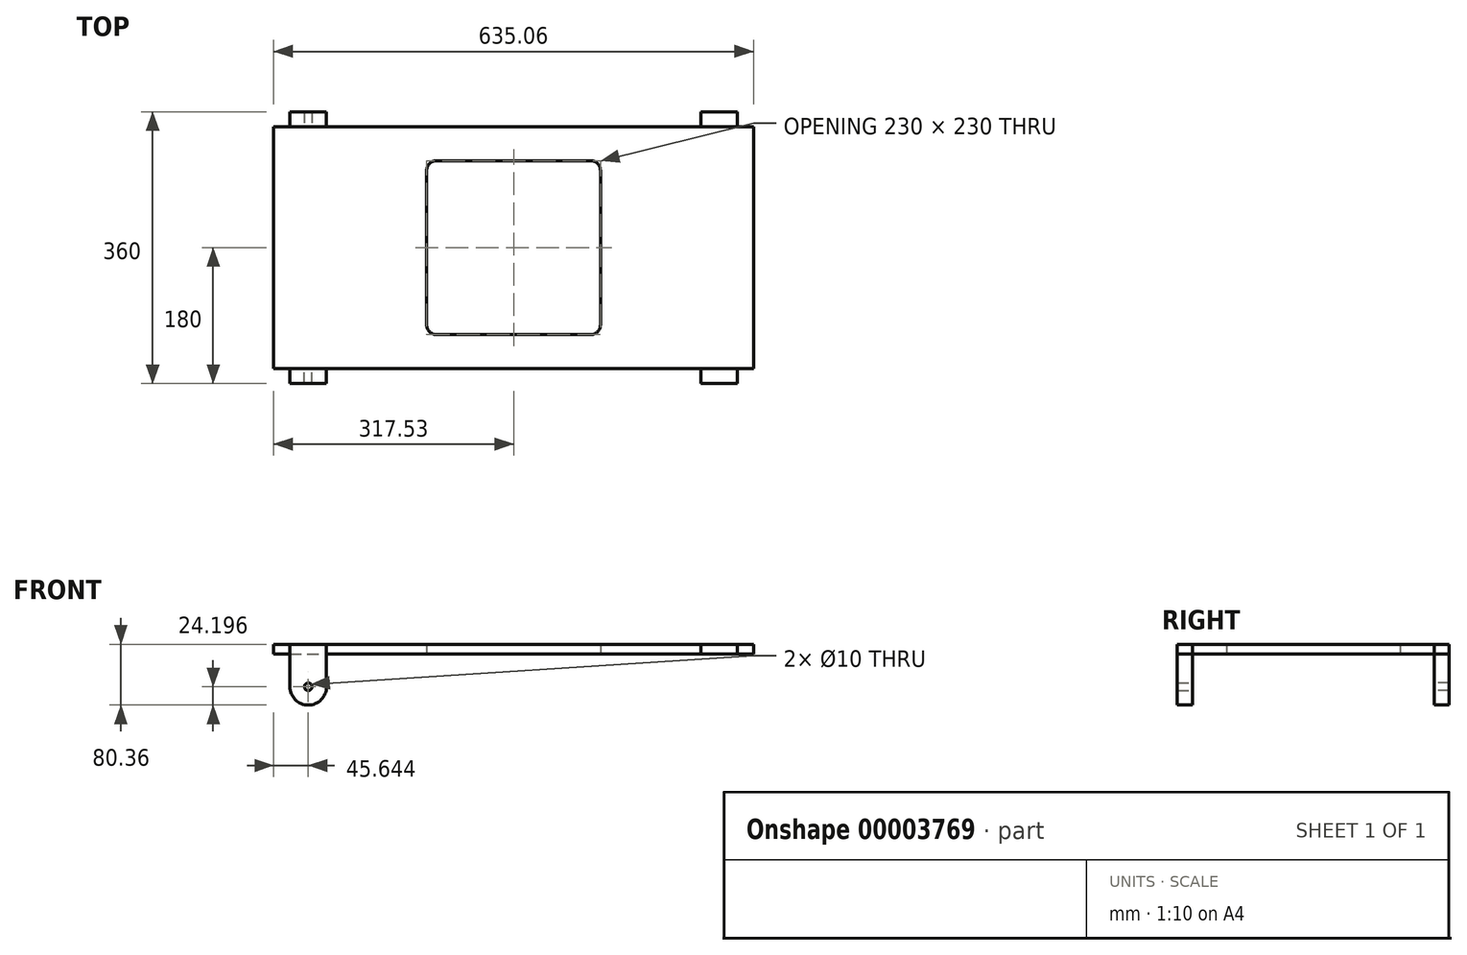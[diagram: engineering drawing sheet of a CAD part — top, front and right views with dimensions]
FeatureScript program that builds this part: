
annotation { "Feature Type Name" : "Feature", "Feature Type Description" : "" }
export const myFeature = defineFeature(function(context is Context, id is Id, definition is map)
    precondition{}
    {
        {
            var Q0;
            Q0=qCreatedBy(makeId("Top.planeOp"),FACE);
            var sketch = newSketch(context, id + "F0", { "sketchPlane" : qUnion([Q0])});
            skLineSegment(sketch, "E0.rect.bottom", {"start": v(-317.53, 160) * mm, "end": v(317.53, 160) * mm});
            skLineSegment(sketch, "E0.rect.top", {"start": v(-317.53, -160) * mm, "end": v(317.53, -160) * mm});
            skLineSegment(sketch, "E0.rect.left", {"start": v(-317.53, 160) * mm, "end": v(-317.53, -160) * mm});
            skLineSegment(sketch, "E0.rect.right", {"start": v(317.53, 160) * mm, "end": v(317.53, -160) * mm});
            skPoint(sketch, "E0.rect.middle", {"position": v(0, 0) * mm});
            skLineSegment(sketch, "E1.rect.bottom", {"start": v(-102.3, 115) * mm, "end": v(102.3, 115) * mm});
            skLineSegment(sketch, "E1.rect.top", {"start": v(-102.3, -115) * mm, "end": v(102.3, -115) * mm});
            skLineSegment(sketch, "E1.rect.left", {"start": v(-115, 102.3) * mm, "end": v(-115, -102.3) * mm});
            skLineSegment(sketch, "E1.rect.right", {"start": v(115, 102.3) * mm, "end": v(115, -102.3) * mm});
            skPoint(sketch, "E2.visualSharp", {"position": v(-115, 115) * mm});
            skArc(sketch, "E2.filletArc", {"start": v(-102.3, 115) * mm, "mid": v(-111.28, 111.28) * mm, "end": v(-115, 102.3) * mm});
            skPoint(sketch, "E3.visualSharp", {"position": v(115, 115) * mm});
            skArc(sketch, "E3.filletArc", {"start": v(115, 102.3) * mm, "mid": v(111.28, 111.28) * mm, "end": v(102.3, 115) * mm});
            skPoint(sketch, "E4.visualSharp", {"position": v(115, -115) * mm});
            skArc(sketch, "E4.filletArc", {"start": v(102.3, -115) * mm, "mid": v(111.28, -111.28) * mm, "end": v(115, -102.3) * mm});
            skPoint(sketch, "E5.visualSharp", {"position": v(-115, -115) * mm});
            skArc(sketch, "E5.filletArc", {"start": v(-115, -102.3) * mm, "mid": v(-111.28, -111.28) * mm, "end": v(-102.3, -115) * mm});
            skSolve(sketch);
        }
        {
            var Q0;
            Q0=makeQuery(id+"F0.imprint","IMPRINT",FACE,{"disambiguationData":[TD([[makeQuery(id+"F0.imprint","IMPRINT",EDGE,{"derivedFrom":sQuery(id+"F0.wireOp",EDGE,"E0.rect.bottom")}),-1.0]])]});
            extrude(context, id + "F1", {"entities" : qUnion([Q0]), "depth" : 12.7 * mm});
        }
        {
            var Q0;
            Q0=makeQuery(id+"F1.opExtrude","SWEPT_FACE",FACE,{"disambiguationData":[OSD([sQuery(id+"F0.wireOp",EDGE,"E0.rect.top")])]});
            var sketch = newSketch(context, id + "F2", { "sketchPlane" : qUnion([Q0])});
            skArc(sketch, "E6", {"start": v(-296.08, -43.46) * mm, "mid": v(-271.89, -67.66) * mm, "end": v(-247.69, -43.46) * mm});
            skLineSegment(sketch, "E7", {"start": v(-296.08, -43.46) * mm, "end": v(-296.08, 12.7) * mm});
            skLineSegment(sketch, "E8", {"start": v(-247.69, -43.46) * mm, "end": v(-247.69, 12.7) * mm});
            skCircle(sketch, "E9", {"center": v(-271.89, -43.46) * mm, "radius": 5 * mm});
            skLineSegment(sketch, "E10", {"start": v(0, 12.7) * mm, "end": v(0, 0) * mm, "construction": true});
            skLineSegment(sketch, "E11.0.MirrorCS", {"start": v(296.08, -43.46) * mm, "end": v(296.08, 12.7) * mm});
            skArc(sketch, "E12.0.MirrorCS", {"start": v(296.08, -43.46) * mm, "mid": v(271.89, -67.66) * mm, "end": v(247.69, -43.46) * mm});
            skLineSegment(sketch, "E13.0.MirrorCS", {"start": v(247.69, -43.46) * mm, "end": v(247.69, 12.7) * mm});
            skCircle(sketch, "E14.0.MirrorC", {"center": v(271.89, -43.46) * mm, "radius": 5 * mm});
            skSolve(sketch);
        }
        {
            var Q0;
            {var subQ0=sQuery(id+"F0.wireOp",EDGE,"E0.rect.top");var subQ4=sQuery(id+"F2.wireOp",EDGE,"E7");var subQ6=makeQuery(id+"F1.opExtrude","CAP_EDGE",EDGE,{"disambiguationData":[OSD([subQ0])],"isStart":false});var subQ8=makeQuery(id+"F2.imprint","INTERSECT",VERTEX,{"derivedFrom":[subQ6,subQ4]});Q0=makeQuery(id+"F2.imprint","IMPRINT",FACE,{"disambiguationData":[TD([[makeQuery(id+"F2.imprint","IMPRINT",EDGE,{"disambiguationData":[TD([[subQ8,1.0]])],"derivedFrom":subQ4}),-1.0]])]});}
            var Q1;
            {var subQ5=sQuery(id+"F2.wireOp",EDGE,"E6");Q1=makeQuery(id+"F2.imprint","IMPRINT",FACE,{"disambiguationData":[TD([[makeQuery(id+"F2.imprint","IMPRINT",EDGE,{"derivedFrom":subQ5}),1.0]])]});}
            var Q2;
            {var subQ0=sQuery(id+"F0.wireOp",EDGE,"E0.rect.top");var subQ4=sQuery(id+"F2.wireOp",EDGE,"E11.0.MirrorCS");var subQ6=makeQuery(id+"F1.opExtrude","CAP_EDGE",EDGE,{"disambiguationData":[OSD([subQ0])],"isStart":false});var subQ8=makeQuery(id+"F2.imprint","INTERSECT",VERTEX,{"derivedFrom":[subQ6,subQ4]});Q2=makeQuery(id+"F2.imprint","IMPRINT",FACE,{"disambiguationData":[TD([[makeQuery(id+"F2.imprint","IMPRINT",EDGE,{"disambiguationData":[TD([[subQ8,1.0]])],"derivedFrom":subQ4}),1.0]])]});}
            var Q3;
            {var subQ3=sQuery(id+"F2.wireOp",EDGE,"E12.0.MirrorCS");Q3=makeQuery(id+"F2.imprint","IMPRINT",FACE,{"disambiguationData":[TD([[makeQuery(id+"F2.imprint","IMPRINT",EDGE,{"derivedFrom":subQ3}),-1.0]])]});}
            extrude(context, id + "F3", {"entities" : qUnion([Q0, Q1, Q2, Q3]), "depth" : 20 * mm});
        }
        {
            var Q0;
            Q0=makeQuery(id+"F3.opExtrude","SWEPT_BODY",BODY,{"disambiguationData":[OSD([sQuery(id+"F0.wireOp",EDGE,"E0.rect.top"),sQuery(id+"F2.wireOp",EDGE,"E6"),sQuery(id+"F2.wireOp",EDGE,"E7"),sQuery(id+"F2.wireOp",EDGE,"E8"),sQuery(id+"F2.wireOp",EDGE,"E9")])]});
            var Q1;
            Q1=qCreatedBy(makeId("Front.planeOp"),FACE);
            mirror(context, id + "F4", {"entities" : qUnion([Q0]), "mirrorPlane" : qUnion([Q1])});
        }
        {
            var Q0;
            Q0=makeQuery(id+"F3.opExtrude","SWEPT_BODY",BODY,{"disambiguationData":[OSD([sQuery(id+"F0.wireOp",EDGE,"E0.rect.top"),sQuery(id+"F2.wireOp",EDGE,"E11.0.MirrorCS"),sQuery(id+"F2.wireOp",EDGE,"E12.0.MirrorCS"),sQuery(id+"F2.wireOp",EDGE,"E13.0.MirrorCS"),sQuery(id+"F2.wireOp",EDGE,"E14.0.MirrorC")])]});
            var Q1;
            Q1=qCreatedBy(makeId("Front.planeOp"),FACE);
            mirror(context, id + "F5", {"entities" : qUnion([Q0]), "mirrorPlane" : qUnion([Q1])});
        }
        {
            var Q0;
            Q0=makeQuery(id+"F5.opPattern","COPY",FACE,{"derivedFrom":makeQuery(id+"F3.opExtrude","CAP_FACE",FACE,{"disambiguationData":[OSD([sQuery(id+"F0.wireOp",EDGE,"E0.rect.top"),sQuery(id+"F2.wireOp",EDGE,"E11.0.MirrorCS"),sQuery(id+"F2.wireOp",EDGE,"E12.0.MirrorCS"),sQuery(id+"F2.wireOp",EDGE,"E13.0.MirrorCS"),sQuery(id+"F2.wireOp",EDGE,"E14.0.MirrorC")])],"isStart":false}),"instanceName":"1"});
            var sketch = newSketch(context, id + "F6", { "sketchPlane" : qUnion([Q0])});
            skCircle(sketch, "E15", {"center": v(-271.89, -43.46) * mm, "radius": 5 * mm});
            skCircle(sketch, "E16.0.MirrorC", {"center": v(271.89, -43.46) * mm, "radius": 5 * mm});
            skSolve(sketch);
        }
        {
            var Q0;
            Q0=makeQuery(id+"F6.imprint","IMPRINT",FACE,{"disambiguationData":[TD([[makeQuery(id+"F6.imprint","IMPRINT",EDGE,{"derivedFrom":sQuery(id+"F6.wireOp",EDGE,"E15")}),1.0]])]});
            var Q1;
            Q1=makeQuery(id+"F6.imprint","IMPRINT",FACE,{"disambiguationData":[TD([[makeQuery(id+"F6.imprint","IMPRINT",EDGE,{"derivedFrom":sQuery(id+"F6.wireOp",EDGE,"E16.0.MirrorC")}),-1.0]])]});
            extrude(context, id + "F7", {"entities" : qUnion([Q0, Q1]), "oppositeDirection" : true, "depth" : 400 * mm});
        }
        {
            var Q0;
            Q0=makeQuery(id+"F7.opExtrude","SWEPT_BODY",BODY,{"disambiguationData":[OSD([sQuery(id+"F6.wireOp",EDGE,"E16.0.MirrorC")])]});
            var Q1;
            Q1=makeQuery(id+"F7.opExtrude","SWEPT_BODY",BODY,{"disambiguationData":[OSD([sQuery(id+"F6.wireOp",EDGE,"E15")])]});
            deleteBodies(context, id + "F8", {"entities" : qUnion([Q0, Q1])});
        }
    });
